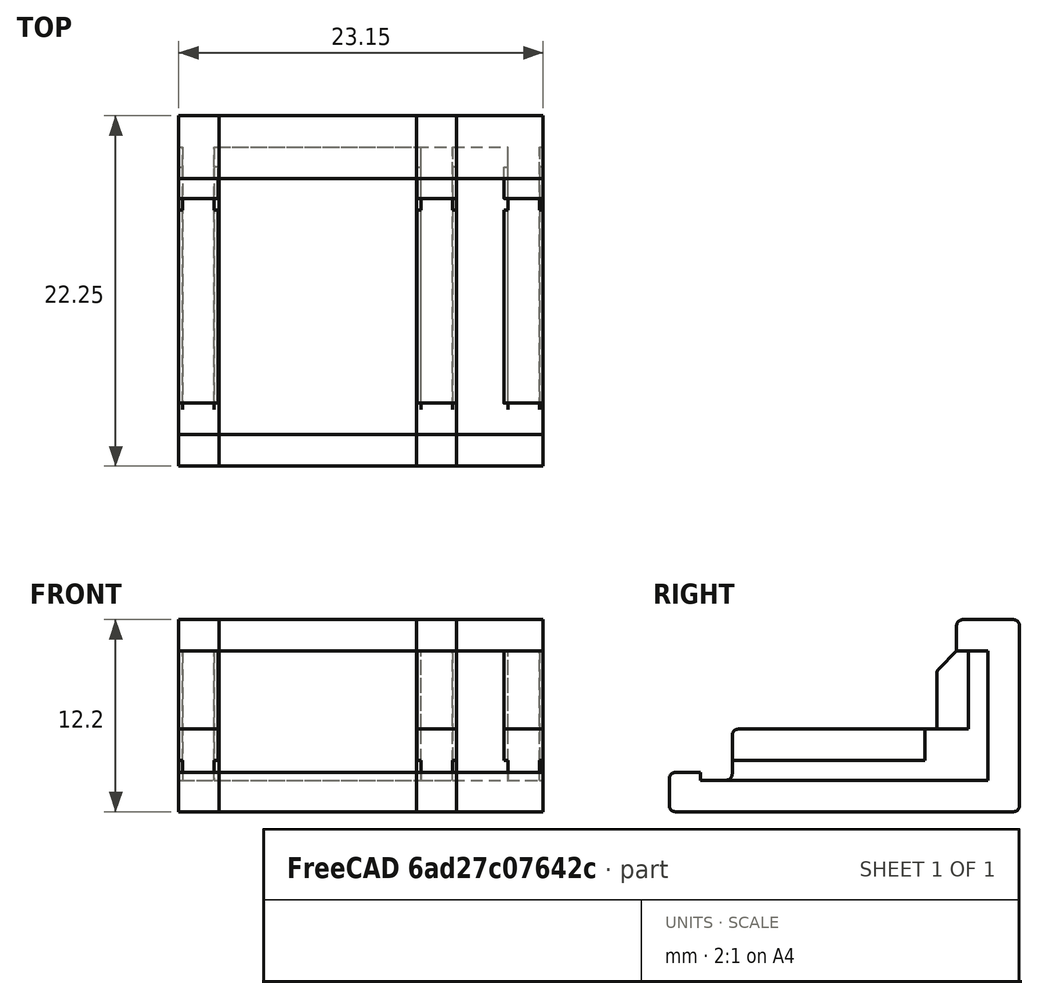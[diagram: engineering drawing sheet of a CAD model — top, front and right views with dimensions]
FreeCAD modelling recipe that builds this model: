
FCSTD DOCUMENT  (FreeCAD 0.18R16146 (Git))
Label: wago-template
License: Other
LicenseURL: GPL3
objects: Part::Feature×6, Part::Box×2, Part::MultiCommon×2, Part::MultiFuse×2
note: 12 computed .brp shape members not serialized (recipe doc carries the construction recipe); baked Part::Feature solids carry a one-line shape summary decoded from their .brp

FEATURE [Part::Feature] Part__Feature  label="v2_bed_wago v1"
  shape: bbox 130 x 22.25 x 15.78 mm, 368 faces (baked)
FEATURE [Part::Box] Box  label="Cube"
  AttacherType = Attacher::AttachEngine3D
  Height = 15
  Length = 15.1
  Placement = pos=(45.7,-19,-6) rot=(0,0,1;0rad)
  Width = 32
FEATURE [Part::Box] Box001  label="Cube001"
  AttacherType = Attacher::AttachEngine3D
  Height = 15
  Length = 15.1
  Placement = pos=(48.25,-19,-6) rot=(0,0,1;0rad)
  Width = 32
FEATURE [Part::Feature] Part__Feature001  label="v2_bed_wago v002"
  shape: bbox 130 x 22.25 x 15.78 mm, 368 faces (baked)
FEATURE [Part::MultiCommon] Common001  label="left"
  Shapes = -> [Part__Feature,Box]
FEATURE [Part::MultiCommon] Common  label="right"
  Shapes = -> [Part__Feature001,Box001]
FEATURE [Part::Feature] Common002  label="right001"
  shape: bbox 15.1 x 22.25 x 12.2 mm, 40 faces (baked)
FEATURE [Part::Feature] Common001001  label="left001"
  shape: bbox 15.1 x 22.25 x 12.2 mm, 39 faces (baked)
FEATURE [Part::MultiFuse] Fusion  label="wago-2"
  Shapes = -> [Common001001,Common002]
FEATURE [Part::Feature] Common001002  label="right002"
  Placement = pos=(5.5,0,0) rot=(0,0,1;0rad)
  shape: bbox 15.1 x 22.25 x 12.2 mm, 40 faces (baked)
FEATURE [Part::Feature] Common001003  label="left002"
  shape: bbox 15.1 x 22.25 x 12.2 mm, 39 faces (baked)
FEATURE [Part::MultiFuse] Fusion001  label="wago-3"
  Shapes = -> [Common001002,Common001003]
